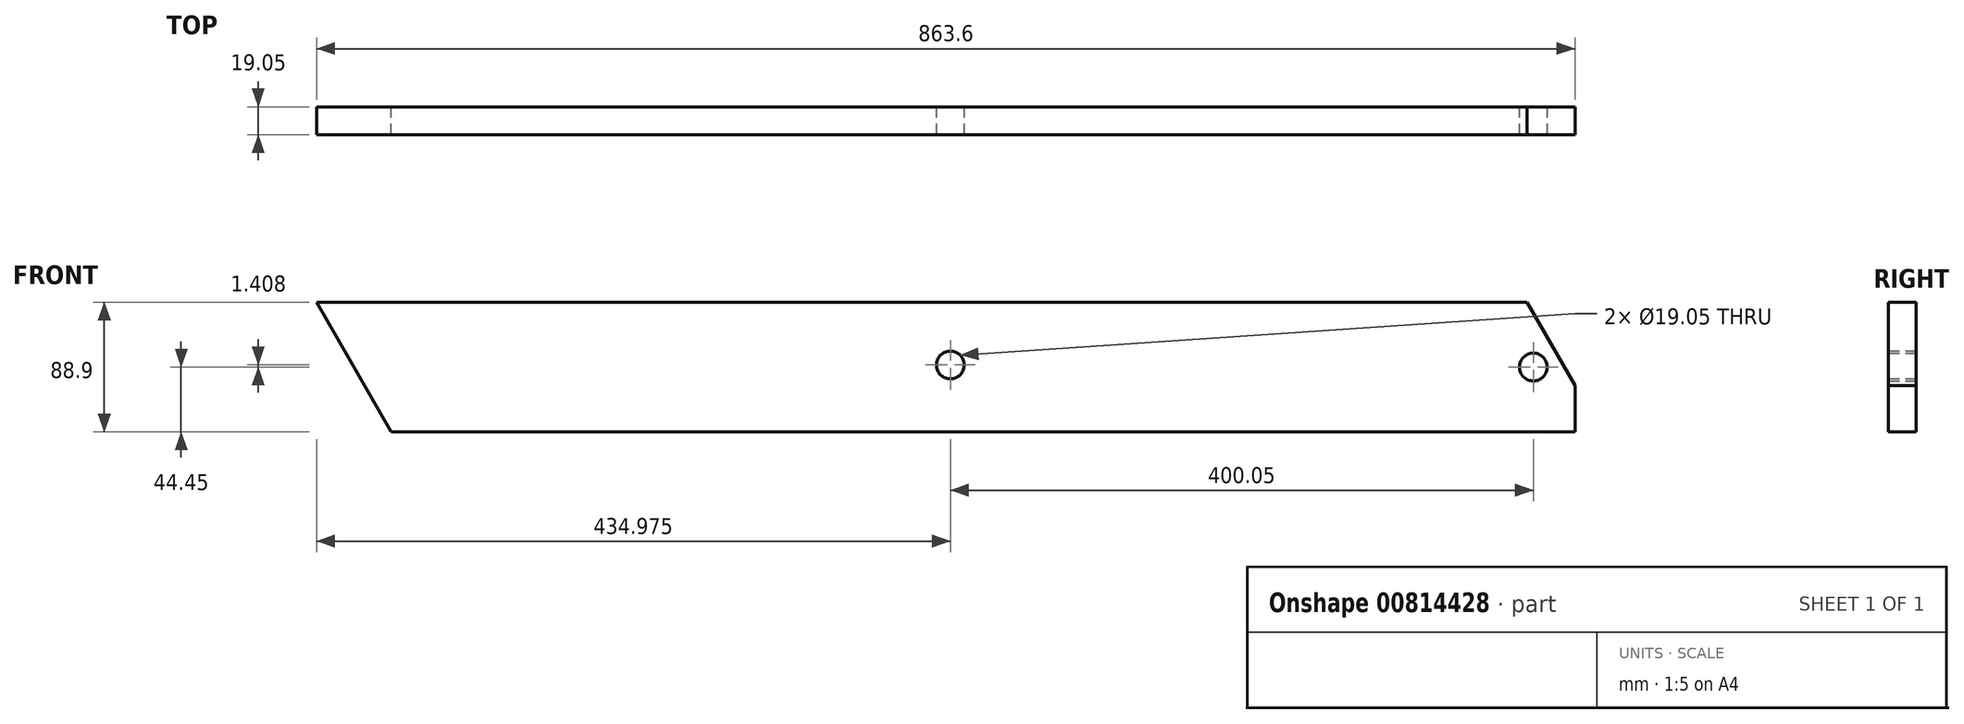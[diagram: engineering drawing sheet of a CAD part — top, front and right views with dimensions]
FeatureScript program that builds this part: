
annotation { "Feature Type Name" : "Feature", "Feature Type Description" : "" }
export const myFeature = defineFeature(function(context is Context, id is Id, definition is map)
    precondition{}
    {
        {
            var Q0;
            Q0=qCreatedBy(makeId("Front.planeOp"),FACE);
            var sketch = newSketch(context, id + "F0", { "sketchPlane" : qUnion([Q0])});
            skLineSegment(sketch, "E0", {"start": v(0, 0) * mm, "end": v(-812.27, 0) * mm});
            skLineSegment(sketch, "E1", {"start": v(0, 0) * mm, "end": v(0, 31.75) * mm});
            skLineSegment(sketch, "E2", {"start": v(-812.27, 0) * mm, "end": v(-863.6, 88.9) * mm});
            skLineSegment(sketch, "E3", {"start": v(-863.6, 88.9) * mm, "end": v(-33, 88.9) * mm});
            skLineSegment(sketch, "E4", {"start": v(-33, 88.9) * mm, "end": v(0, 31.75) * mm});
            skSolve(sketch);
        }
        {
            var Q0;
            Q0=makeQuery(id+"F0.imprint","IMPRINT",FACE,{"disambiguationData":[TD([[makeQuery(id+"F0.imprint","IMPRINT",EDGE,{"derivedFrom":sQuery(id+"F0.wireOp",EDGE,"E0")}),-1.0]])]});
            var Q1;
            Q1 = qSketchRegion(id + "F0", true);
            extrude(context, id + "F1", {"entities" : qUnion([Q0, Q1]), "depth" : 19.05 * mm, "offsetDistance" : 25.4 * mm});
        }
        {
            var Q0;
            Q0=qCreatedBy(makeId("Front.planeOp"),FACE);
            var sketch = newSketch(context, id + "F2", { "sketchPlane" : qUnion([Q0])});
            skCircle(sketch, "E5", {"center": v(-28.58, 44.45) * mm, "radius": 9.53 * mm});
            skSolve(sketch);
        }
        {
            var Q0;
            Q0=sQuery(id+"F2.wireOp",VERTEX,"E5.center");
            var Q1;
            Q1=makeQuery(id+"F1.opExtrude","SWEPT_BODY",BODY,{"disambiguationData":[OSD([sQuery(id+"F0.wireOp",EDGE,"E0"),sQuery(id+"F0.wireOp",EDGE,"E1"),sQuery(id+"F0.wireOp",EDGE,"E2"),sQuery(id+"F0.wireOp",EDGE,"E3"),sQuery(id+"F0.wireOp",EDGE,"E4")])]});
            hole(context, id + "F3", {"style" : HoleStyle.SIMPLE, "endStyle" : HoleEndStyle.THROUGH, "oppositeDirection" : true, "holeDiameter" : 19.05 * mm, "majorDiameter" : 6.35 * mm, "isTappedThrough" : true, "tappedDepth" : 12.7 * mm, "tapClearance" : 3, "locations" : qUnion([Q0]), "scope" : qUnion([Q1])});
        }
        {
            var Q0;
            Q0=qCreatedBy(makeId("Front.planeOp"),FACE);
            var sketch = newSketch(context, id + "F4", { "sketchPlane" : qUnion([Q0])});
            skCircle(sketch, "E6", {"center": v(-428.63, 45.86) * mm, "radius": 9.53 * mm});
            skSolve(sketch);
        }
        {
            var Q0;
            Q0=sQuery(id+"F4.wireOp",VERTEX,"E6.center");
            var Q1;
            Q1=makeQuery(id+"F1.opExtrude","SWEPT_BODY",BODY,{"disambiguationData":[OSD([sQuery(id+"F0.wireOp",EDGE,"E0"),sQuery(id+"F0.wireOp",EDGE,"E1"),sQuery(id+"F0.wireOp",EDGE,"E2"),sQuery(id+"F0.wireOp",EDGE,"E3"),sQuery(id+"F0.wireOp",EDGE,"E4")])]});
            hole(context, id + "F5", {"style" : HoleStyle.SIMPLE, "endStyle" : HoleEndStyle.THROUGH, "oppositeDirection" : true, "holeDiameter" : 19.05 * mm, "majorDiameter" : 6.35 * mm, "isTappedThrough" : true, "tappedDepth" : 12.7 * mm, "tapClearance" : 3, "locations" : qUnion([Q0]), "scope" : qUnion([Q1])});
        }
    });
